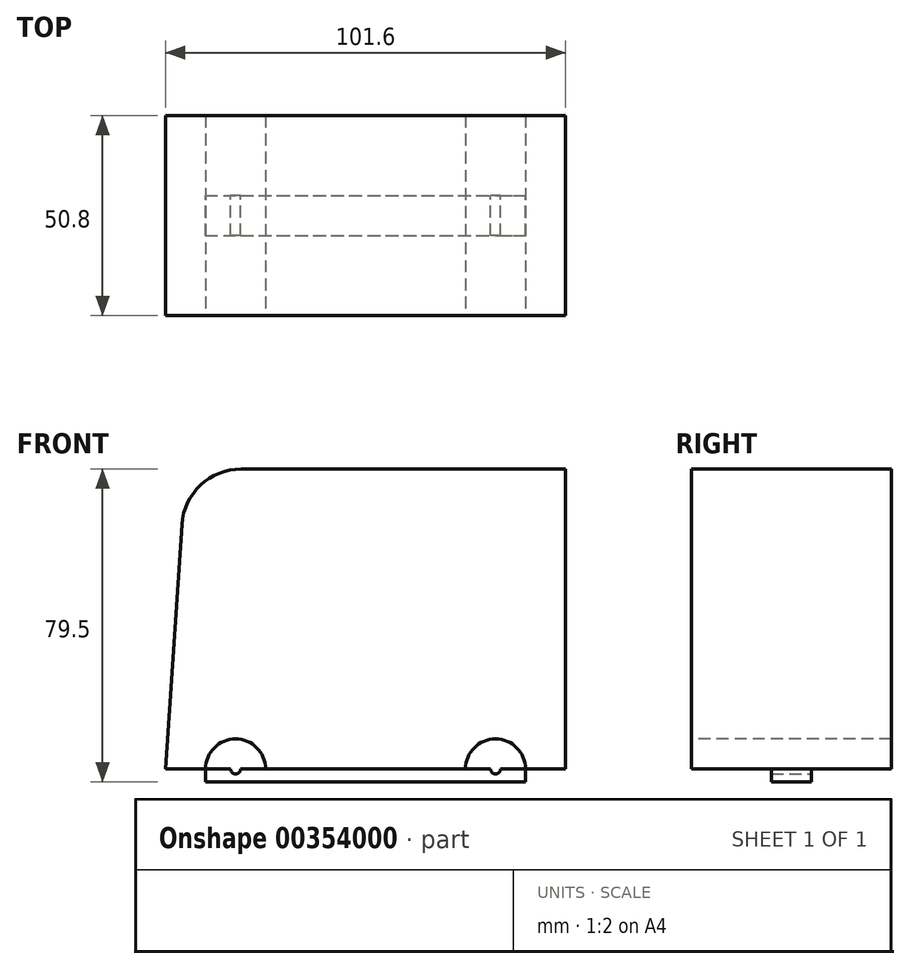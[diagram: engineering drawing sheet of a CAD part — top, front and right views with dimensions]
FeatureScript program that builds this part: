
annotation { "Feature Type Name" : "Feature", "Feature Type Description" : "" }
export const myFeature = defineFeature(function(context is Context, id is Id, definition is map)
    precondition{}
    {
        {
            var Q0;
            Q0=qCreatedBy(makeId("Top.planeOp"),FACE);
            var sketch = newSketch(context, id + "F0", { "sketchPlane" : qUnion([Q0])});
            skLineSegment(sketch, "E0.bottom", {"start": v(-20.29, 34.26) * mm, "end": v(81.31, 34.26) * mm});
            skLineSegment(sketch, "E0.top", {"start": v(-20.29, -16.54) * mm, "end": v(81.31, -16.54) * mm});
            skLineSegment(sketch, "E0.left", {"start": v(-20.29, 34.26) * mm, "end": v(-20.29, -16.54) * mm});
            skLineSegment(sketch, "E0.right", {"start": v(81.31, 34.26) * mm, "end": v(81.31, -16.54) * mm});
            skSolve(sketch);
        }
        {
            var Q0;
            Q0 = qSketchRegion(id + "F0", true);
            extrude(context, id + "F1", {"entities" : qUnion([Q0]), "depth" : 76.2 * mm});
        }
        {
            var Q0;
            Q0=makeQuery(id+"F1.opExtrude","SWEPT_FACE",FACE,{"disambiguationData":[OSD([sQuery(id+"F0.wireOp",EDGE,"E0.top")])]});
            var sketch = newSketch(context, id + "F2", { "sketchPlane" : qUnion([Q0])});
            skArc(sketch, "E1", {"start": v(5.11, 0) * mm, "mid": v(-2.5, 7.62) * mm, "end": v(-10.13, 0) * mm});
            skArc(sketch, "E2", {"start": v(71.15, 0) * mm, "mid": v(63.53, 7.62) * mm, "end": v(55.91, 0) * mm});
            skLineSegment(sketch, "E3", {"start": v(-2.5, 0) * mm, "end": v(-10.13, 0) * mm});
            skLineSegment(sketch, "E4", {"start": v(-10.13, 0) * mm, "end": v(5.11, 0) * mm});
            skLineSegment(sketch, "E5", {"start": v(63.53, 0) * mm, "end": v(55.91, 0) * mm});
            skLineSegment(sketch, "E6", {"start": v(55.91, 0) * mm, "end": v(71.15, 0) * mm});
            skSolve(sketch);
        }
        {
            var Q0;
            Q0 = qSketchRegion(id + "F2", true);
            extrude(context, id + "F3", {"entities" : qUnion([Q0]), "operationType" : NewBodyOperationType.REMOVE, "oppositeDirection" : true, "depth" : 50.8 * mm});
        }
        {
            var Q0;
            {var subQ0=sQuery(id+"F0.wireOp",EDGE,"E0.bottom");var subQ1=sQuery(id+"F0.wireOp",EDGE,"E0.top");Q0=makeQuery(id+"F3.boolean.opBoolean","SPLIT",FACE,{"disambiguationData":[TD([makeQuery(id+"F1.opExtrude","SWEPT_FACE",FACE,{"disambiguationData":[OSD([subQ0])]}),makeQuery(id+"F1.opExtrude","SWEPT_FACE",FACE,{"disambiguationData":[OSD([subQ1])]}),makeQuery(id+"F3.opExtrude","SWEPT_FACE",FACE,{"disambiguationData":[OSD([sQuery(id+"F2.wireOp",EDGE,"E1")])]}),makeQuery(id+"F3.opExtrude","SWEPT_FACE",FACE,{"disambiguationData":[OSD([sQuery(id+"F2.wireOp",EDGE,"E2")])]})])],"derivedFrom":makeQuery(id+"F1.opExtrude","CAP_FACE",FACE,{"disambiguationData":[OSD([subQ0,subQ1,sQuery(id+"F0.wireOp",EDGE,"E0.left"),sQuery(id+"F0.wireOp",EDGE,"E0.right")])],"isStart":true})});}
            var sketch = newSketch(context, id + "F4", { "sketchPlane" : qUnion([Q0])});
            skLineSegment(sketch, "E7.bottom", {"start": v(-10.13, -3.78) * mm, "end": v(71.15, -3.78) * mm});
            skLineSegment(sketch, "E7.top", {"start": v(-10.13, -13.94) * mm, "end": v(71.15, -13.94) * mm});
            skLineSegment(sketch, "E7.left", {"start": v(-10.13, -3.78) * mm, "end": v(-10.13, -13.94) * mm});
            skLineSegment(sketch, "E7.right", {"start": v(71.15, -3.78) * mm, "end": v(71.15, -13.94) * mm});
            skSolve(sketch);
        }
        {
            var Q0;
            Q0 = qSketchRegion(id + "F4", true);
            extrude(context, id + "F5", {"entities" : qUnion([Q0]), "depth" : 3.3 * mm});
        }
        {
            var Q0;
            Q0=makeQuery(id+"F5.opExtrude","SWEPT_FACE",FACE,{"disambiguationData":[OSD([sQuery(id+"F4.wireOp",EDGE,"E7.top")])]});
            var sketch = newSketch(context, id + "F6", { "sketchPlane" : qUnion([Q0])});
            skCircle(sketch, "E8", {"center": v(-63.53, 0) * mm, "radius": 1.27 * mm});
            skCircle(sketch, "E9", {"center": v(2.5, 0) * mm, "radius": 1.27 * mm});
            skSolve(sketch);
        }
        {
            var Q0;
            Q0 = qSketchRegion(id + "F6", true);
            extrude(context, id + "F7", {"entities" : qUnion([Q0]), "operationType" : NewBodyOperationType.REMOVE, "oppositeDirection" : true, "depth" : 10.16 * mm});
        }
        {
            var Q0;
            Q0=makeQuery(id+"F1.opExtrude","CAP_EDGE",EDGE,{"disambiguationData":[OSD([sQuery(id+"F0.wireOp",EDGE,"E0.left")])],"isStart":false});
            chamfer(context, id + "F8", {"entities" : qUnion([Q0]), "chamferType" : ChamferType.TWO_OFFSETS, "width1" : 5.08 * mm, "oppositeDirection" : false, "width2" : 76.2 * mm, "tangentPropagation" : true});
        }
        {
            var Q0;
            {var subQ0=sQuery(id+"F0.wireOp",EDGE,"E0.left");Q0=makeQuery(id+"F8.opChamfer","BLEND_EDGE",EDGE,{"blendedFrom":[makeQuery(id+"F1.opExtrude","CAP_EDGE",EDGE,{"disambiguationData":[OSD([subQ0])],"isStart":false}),makeQuery(id+"F1.opExtrude","CAP_FACE",FACE,{"disambiguationData":[OSD([sQuery(id+"F0.wireOp",EDGE,"E0.bottom"),sQuery(id+"F0.wireOp",EDGE,"E0.top"),subQ0,sQuery(id+"F0.wireOp",EDGE,"E0.right")])],"isStart":false})],"blendedInto":[makeQuery(id+"F1.opExtrude","CAP_FACE",FACE,{"disambiguationData":[OSD([sQuery(id+"F0.wireOp",EDGE,"E0.bottom"),sQuery(id+"F0.wireOp",EDGE,"E0.top"),subQ0,sQuery(id+"F0.wireOp",EDGE,"E0.right")])],"isStart":false})]});}
            fillet(context, id + "F9", {"entities" : qUnion([Q0]), "radius" : 15.13 * mm, "tangentPropagation" : true, "allowEdgeOverflow" : false});
        }
    });
